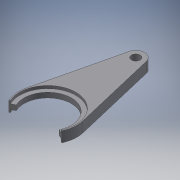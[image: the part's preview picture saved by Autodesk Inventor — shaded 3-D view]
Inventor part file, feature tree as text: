
AUTODESK INVENTOR PART (.ipt)
format: ipt  version: 2017 (Build 210142000, 142)  size: 145,408 bytes
history: native  units: mm
features: extrude x3, sketch x3, plane x1, mirror x1, projected_geometry x1
ambient origin geometry x8: Origin, YZ Plane, XZ Plane, XY Plane, X Axis, Y Axis, Z Axis, Center Point
bodies: Solid1 (feature_tree)
feature tree (9):
  extrude  "Extrusion1"  Depth=8.0mm
  extrude  "Extrusion2"  Depth=8.0mm
  plane  "Work Plane1"
  mirror  "Mirror1"
  extrude  "Extrusion3"  Depth=4.5mm TaperAngle=0.0deg
  sketch  "Sketch1"  dims[d0=43.0mm d1=8.0mm]
  sketch  "Sketch2"  dims[d2=80.0mm d3=8.0mm]
  projected_geometry  "Projected Loop1"
  sketch  "Sketch3"  dims[d4=5.0mm d5=4.5mm d6=0.0mm d7=51.0mm d8=2.5mm d9=0.0mm d10=22.68928mm d11=4.0mm d12=0.0mm]
